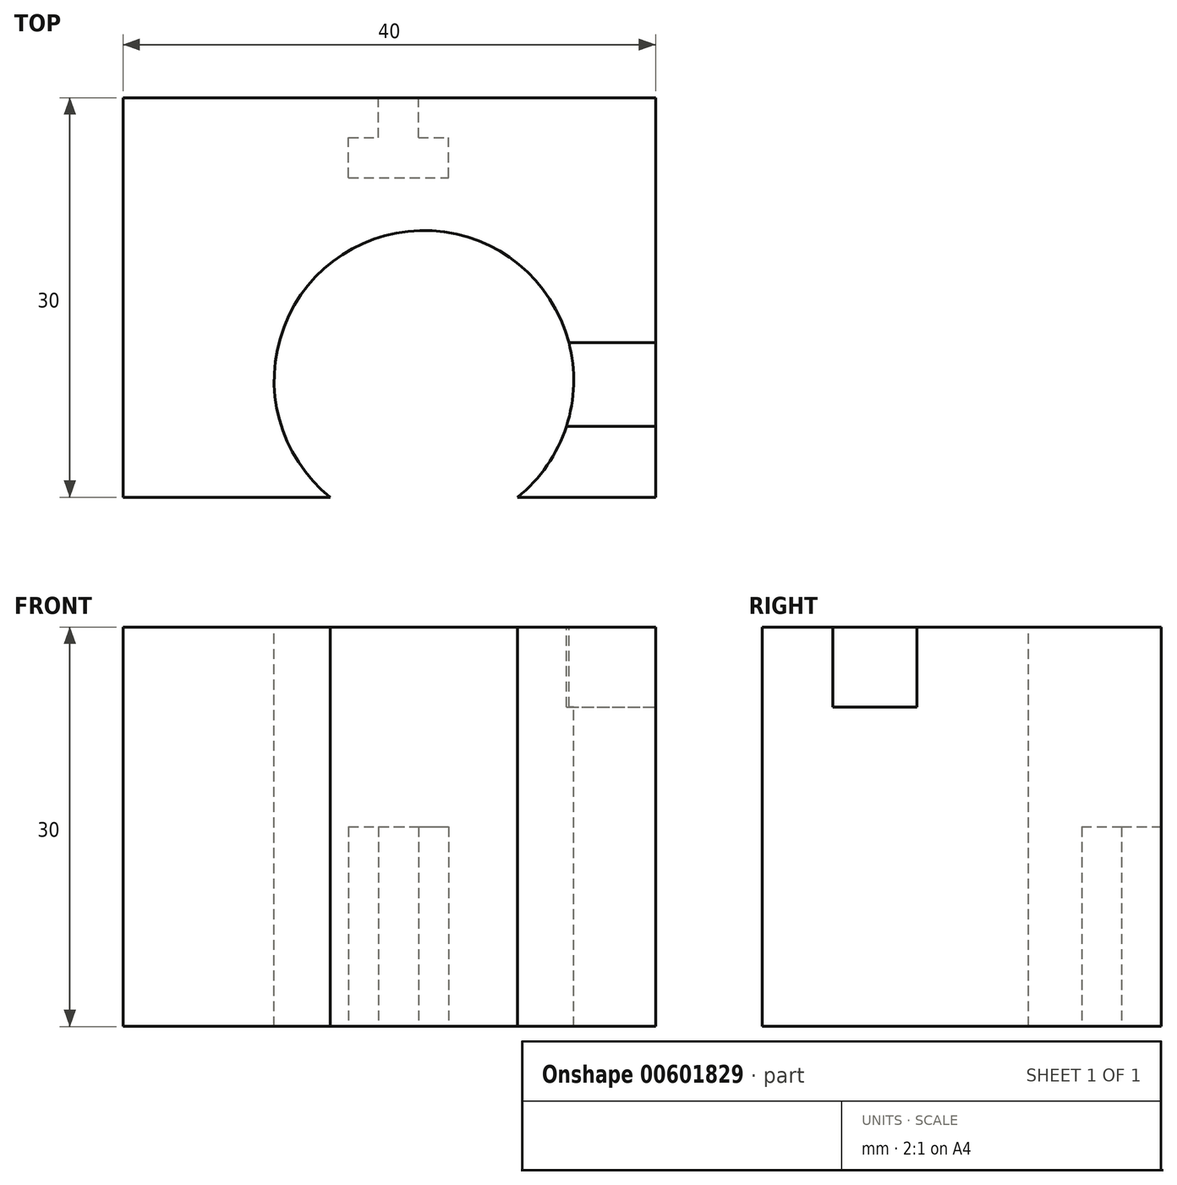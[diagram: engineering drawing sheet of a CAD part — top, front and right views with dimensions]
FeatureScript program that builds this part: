
annotation { "Feature Type Name" : "Feature", "Feature Type Description" : "" }
export const myFeature = defineFeature(function(context is Context, id is Id, definition is map)
    precondition{}
    {
        {
            var Q0;
            Q0=qCreatedBy(makeId("Front.planeOp"),FACE);
            var sketch = newSketch(context, id + "F0", { "sketchPlane" : qUnion([Q0])});
            skLineSegment(sketch, "E0.bottom", {"start": v(-22.6, 15.28) * mm, "end": v(17.4, 15.28) * mm});
            skLineSegment(sketch, "E0.top", {"start": v(-22.6, -14.72) * mm, "end": v(17.4, -14.72) * mm});
            skLineSegment(sketch, "E0.left", {"start": v(-22.6, 15.28) * mm, "end": v(-22.6, -14.72) * mm});
            skLineSegment(sketch, "E0.right", {"start": v(17.4, 15.28) * mm, "end": v(17.4, -14.72) * mm});
            skSolve(sketch);
        }
        {
            var Q0;
            Q0 = qSketchRegion(id + "F0", true);
            extrude(context, id + "F1", {"entities" : qUnion([Q0]), "depth" : 30 * mm, "offsetDistance" : 25 * mm});
        }
        {
            var Q0;
            Q0=makeQuery(id+"F1.opExtrude","SWEPT_FACE",FACE,{"disambiguationData":[OSD([sQuery(id+"F0.wireOp",EDGE,"E0.bottom")])]});
            var sketch = newSketch(context, id + "F2", { "sketchPlane" : qUnion([Q0])});
            skCircle(sketch, "E1", {"center": v(0, -21.22) * mm, "radius": 11.25 * mm});
            skLineSegment(sketch, "E2", {"start": v(0, -21.22) * mm, "end": v(28.43, -21.22) * mm, "construction": true});
            skSolve(sketch);
        }
        {
            var Q0;
            Q0 = qSketchRegion(id + "F2", true);
            extrude(context, id + "F3", {"entities" : qUnion([Q0]), "operationType" : NewBodyOperationType.REMOVE, "oppositeDirection" : true, "depth" : 30 * mm, "offsetDistance" : 25 * mm});
        }
        {
            var Q0;
            Q0=makeQuery(id+"F1.opExtrude","SWEPT_FACE",FACE,{"disambiguationData":[OSD([sQuery(id+"F0.wireOp",EDGE,"E0.bottom")])]});
            var sketch = newSketch(context, id + "F4", { "sketchPlane" : qUnion([Q0])});
            skLineSegment(sketch, "E3.bottom", {"start": v(3.76, -18.38) * mm, "end": v(26.9, -18.38) * mm});
            skLineSegment(sketch, "E3.top", {"start": v(3.76, -24.68) * mm, "end": v(26.9, -24.68) * mm});
            skLineSegment(sketch, "E3.left", {"start": v(3.76, -18.38) * mm, "end": v(3.76, -24.68) * mm});
            skLineSegment(sketch, "E3.right", {"start": v(26.9, -18.38) * mm, "end": v(26.9, -24.68) * mm});
            skSolve(sketch);
        }
        {
            var Q0;
            Q0 = qSketchRegion(id + "F4", true);
            extrude(context, id + "F5", {"entities" : qUnion([Q0]), "operationType" : NewBodyOperationType.REMOVE, "oppositeDirection" : true, "depth" : 6 * mm, "offsetDistance" : 25 * mm});
        }
        {
            var Q0;
            Q0=makeQuery(id+"F1.opExtrude","SWEPT_FACE",FACE,{"disambiguationData":[OSD([sQuery(id+"F0.wireOp",EDGE,"E0.top")])]});
            var sketch = newSketch(context, id + "F6", { "sketchPlane" : qUnion([Q0])});
            skLineSegment(sketch, "E4.bottom", {"start": v(-5.66, 6) * mm, "end": v(1.84, 6) * mm});
            skLineSegment(sketch, "E4.top", {"start": v(-5.66, 3) * mm, "end": v(-3.4, 3) * mm});
            skLineSegment(sketch, "E4.left", {"start": v(-5.66, 6) * mm, "end": v(-5.66, 3) * mm});
            skLineSegment(sketch, "E4.right", {"start": v(1.84, 6) * mm, "end": v(1.84, 3) * mm});
            skLineSegment(sketch, "E5.top", {"start": v(-3.4, 0) * mm, "end": v(-0.4, 0) * mm});
            skLineSegment(sketch, "E5.left", {"start": v(-3.4, 3) * mm, "end": v(-3.4, 0) * mm});
            skLineSegment(sketch, "E5.right", {"start": v(-0.4, 3) * mm, "end": v(-0.4, 0) * mm});
            skLineSegment(sketch, "E6.trimOffspring", {"start": v(-0.4, 3) * mm, "end": v(1.84, 3) * mm});
            skSolve(sketch);
        }
        {
            var Q0;
            Q0 = qSketchRegion(id + "F6", true);
            extrude(context, id + "F7", {"entities" : qUnion([Q0]), "operationType" : NewBodyOperationType.REMOVE, "oppositeDirection" : true, "depth" : 15 * mm, "offsetDistance" : 25 * mm});
        }
    });
